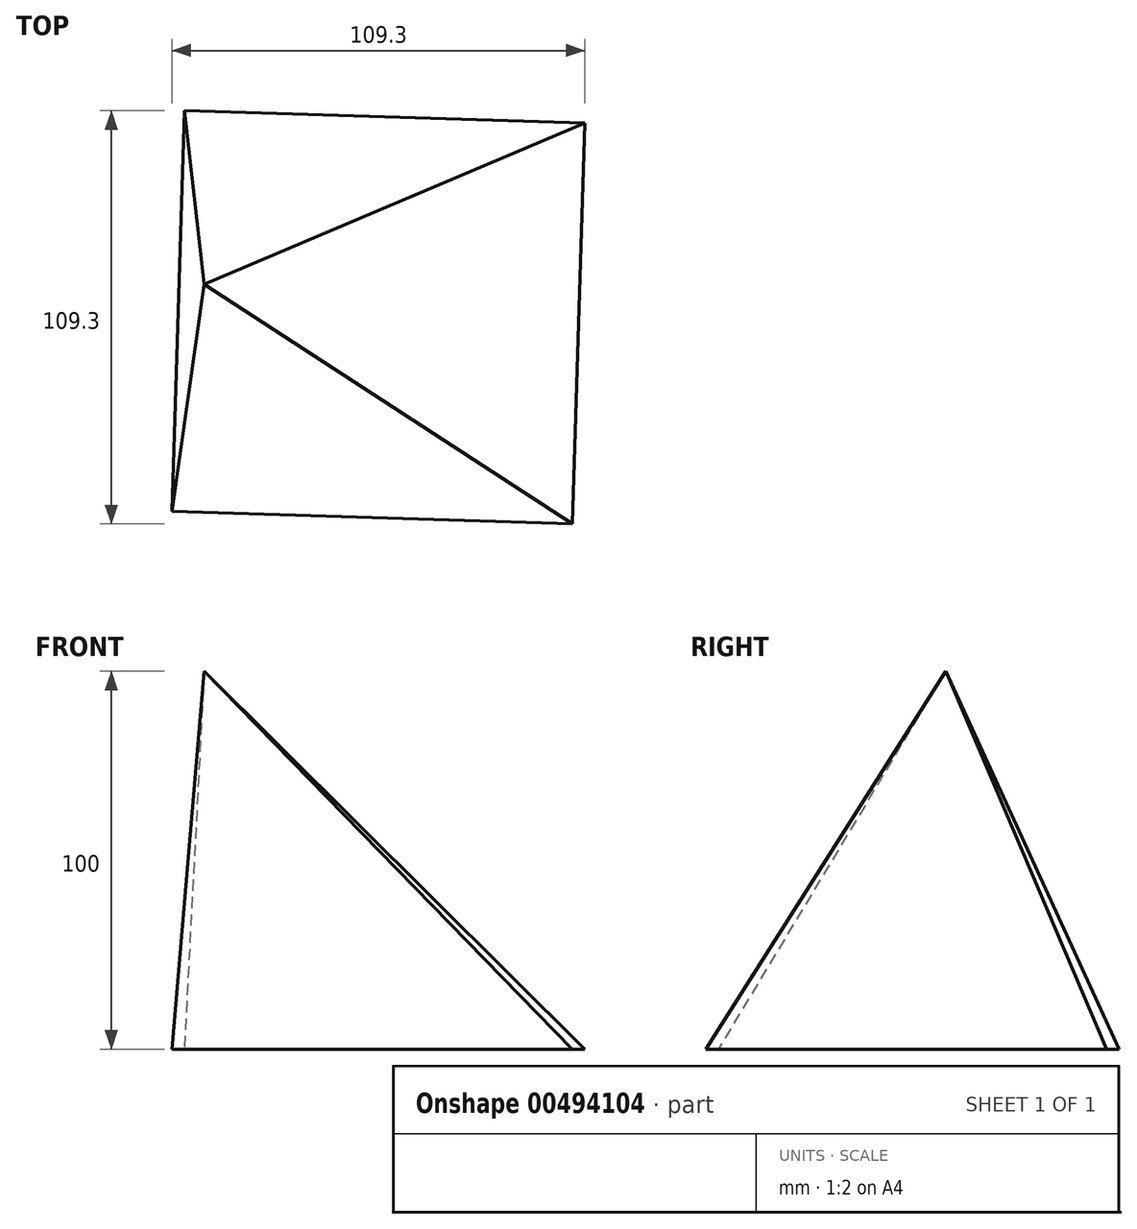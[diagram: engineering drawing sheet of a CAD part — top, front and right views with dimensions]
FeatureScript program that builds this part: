
annotation { "Feature Type Name" : "Feature", "Feature Type Description" : "" }
export const myFeature = defineFeature(function(context is Context, id is Id, definition is map)
    precondition{}
    {
        {
            var Q0;
            Q0=qCreatedBy(makeId("Top.planeOp"),FACE);
            var sketch = newSketch(context, id + "F0", { "sketchPlane" : qUnion([Q0])});
            skCircle(sketch, "E0.cCircle", {"center": v(0, 0) * mm, "radius": 75 * mm, "construction": true});
            skLineSegment(sketch, "E0.0", {"start": v(-51.35, 54.65) * mm, "end": v(54.65, 51.35) * mm});
            skLineSegment(sketch, "E0.1", {"start": v(54.65, 51.35) * mm, "end": v(51.35, -54.65) * mm});
            skLineSegment(sketch, "E0.2", {"start": v(51.35, -54.65) * mm, "end": v(-54.65, -51.35) * mm});
            skLineSegment(sketch, "E0.3", {"start": v(-54.65, -51.35) * mm, "end": v(-51.35, 54.65) * mm});
            skPoint(sketch, "E1", {"position": v(0, -6.17) * mm});
            skSolve(sketch);
        }
        {
            var Q0;
            Q0=qCreatedBy(makeId("Top.planeOp"),FACE);
            cPlane(context, id + "F1", {"entities" : qUnion([Q0]), "cplaneType" : CPlaneType.OFFSET, "offset" : 100 * mm, "width" : 150 * mm, "height" : 150 * mm});
        }
        {
            var Q0;
            Q0=qCreatedBy(id+"F1.planeOp",FACE);
            var sketch = newSketch(context, id + "F2", { "sketchPlane" : qUnion([Q0])});
            skPoint(sketch, "E2", {"position": v(-46.08, 8.8) * mm});
            skSolve(sketch);
        }
        {
            var Q0;
            Q0=sQuery(id+"F2.wireOp",VERTEX,"E2");
            var Q1;
            Q1=makeQuery(id+"F0.imprint","IMPRINT",FACE,{"disambiguationData":[TD([[makeQuery(id+"F0.imprint","IMPRINT",EDGE,{"derivedFrom":sQuery(id+"F0.wireOp",EDGE,"E0.0")}),-1.0]])]});
            loft(context, id + "F3", {"sheetProfilesArray" : [{ "sheetProfileEntities" : qUnion([Q0]) }, { "sheetProfileEntities" : qUnion([Q1]) }]});
        }
    });
